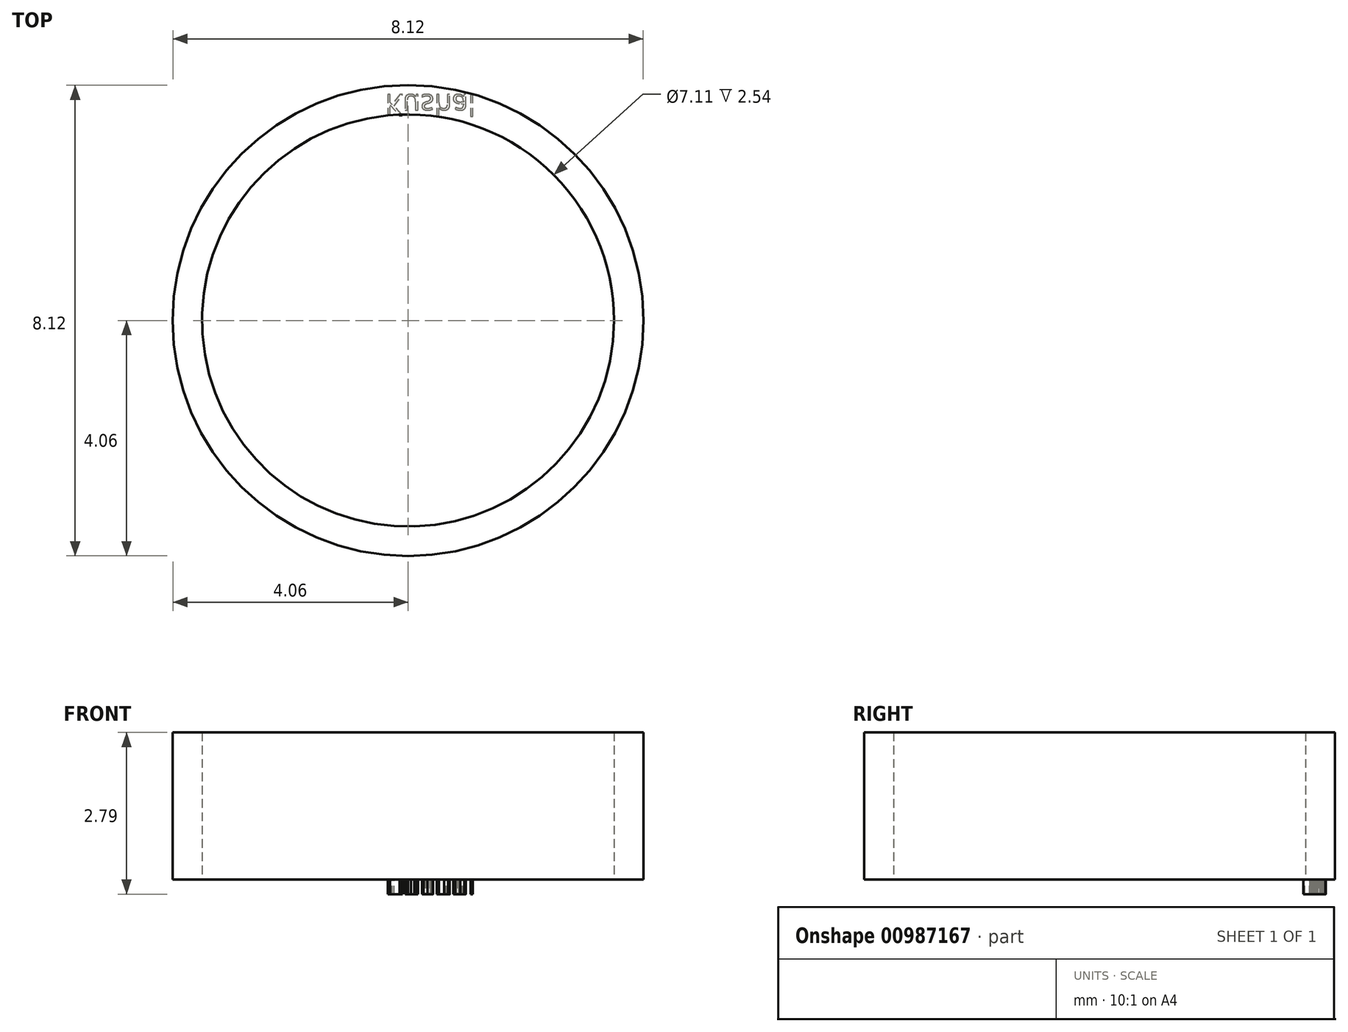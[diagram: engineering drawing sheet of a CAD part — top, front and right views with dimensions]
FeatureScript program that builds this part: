
annotation { "Feature Type Name" : "Feature", "Feature Type Description" : "" }
export const myFeature = defineFeature(function(context is Context, id is Id, definition is map)
    precondition{}
    {
        {
            var Q0;
            Q0=qCreatedBy(makeId("Top.planeOp"),FACE);
            var sketch = newSketch(context, id + "F0", { "sketchPlane" : qUnion([Q0])});
            skCircle(sketch, "E0", {"center": v(0, 0) * mm, "radius": 3.56 * mm});
            skCircle(sketch, "E1", {"center": v(0, 0) * mm, "radius": 4.06 * mm});
            skSolve(sketch);
        }
        {
            var Q0;
            Q0=makeQuery(id+"F0.imprint","IMPRINT",FACE,{"disambiguationData":[TD([[makeQuery(id+"F0.imprint","IMPRINT",EDGE,{"derivedFrom":sQuery(id+"F0.wireOp",EDGE,"E0")}),-1.0]])]});
            extrude(context, id + "F1", {"entities" : qUnion([Q0]), "depth" : 2.54 * mm, "offsetDistance" : 25.4 * mm});
        }
        {
            var Q0;
            Q0=makeQuery(id+"F1.opExtrude","CAP_FACE",FACE,{"disambiguationData":[OSD([sQuery(id+"F0.wireOp",EDGE,"E0"),sQuery(id+"F0.wireOp",EDGE,"E1")])],"isStart":true});
            var sketch = newSketch(context, id + "F2", { "sketchPlane" : qUnion([Q0])});
            skText(sketch, "E2", { "text": "Kushal\n", "fontName": "OpenSans-Regular.ttf"});
            const initialGuessF2  = {"E2": [-0.0004, -0.0039, 1, 0, 0.00036]};
            skSetInitialGuess(sketch, initialGuessF2);
            skSolve(sketch);
        }
        {
            var Q0;
            Q0 = qSketchRegion(id + "F2", true);
            extrude(context, id + "F3", {"entities" : qUnion([Q0]), "operationType" : NewBodyOperationType.ADD, "depth" : 0.25 * mm, "offsetDistance" : 25.4 * mm});
        }
    });
